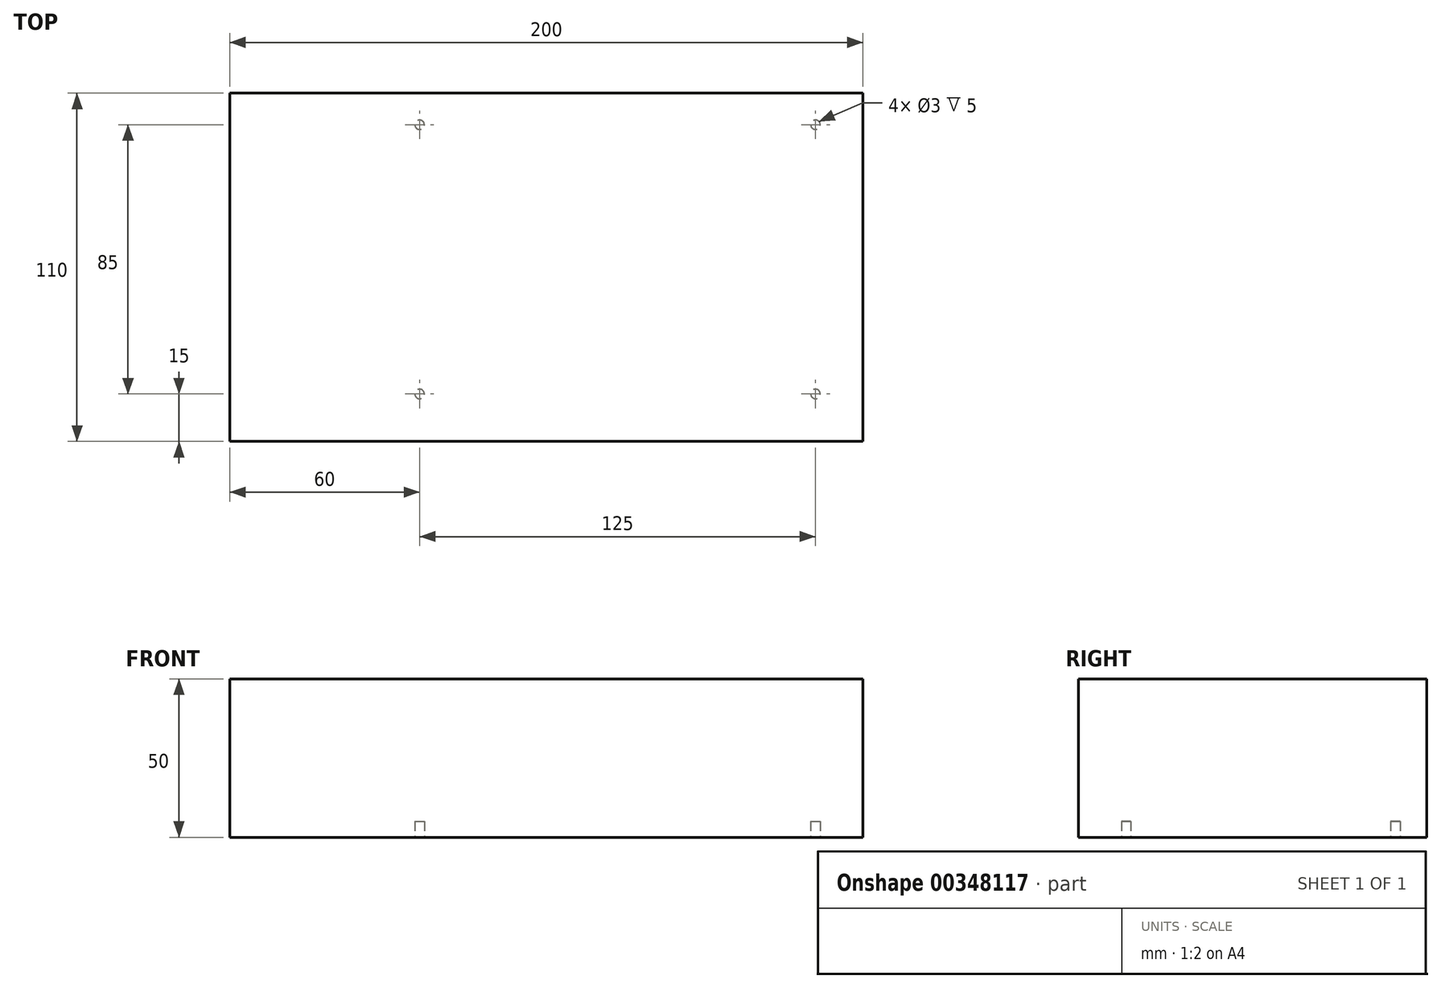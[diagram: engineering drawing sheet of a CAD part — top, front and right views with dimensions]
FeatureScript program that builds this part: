
annotation { "Feature Type Name" : "Feature", "Feature Type Description" : "" }
export const myFeature = defineFeature(function(context is Context, id is Id, definition is map)
    precondition{}
    {
        {
            assignVariable(context, id + "F0", {"name" : "Height", "anyValue" : 50});
        }
        {
            var Q0;
            Q0=qCreatedBy(makeId("Top.planeOp"),FACE);
            var sketch = newSketch(context, id + "F1", { "sketchPlane" : qUnion([Q0])});
            skLineSegment(sketch, "E0.bottom", {"start": v(100, 55) * mm, "end": v(-100, 55) * mm});
            skLineSegment(sketch, "E0.top", {"start": v(100, -55) * mm, "end": v(-100, -55) * mm});
            skLineSegment(sketch, "E0.left", {"start": v(100, 55) * mm, "end": v(100, -55) * mm});
            skLineSegment(sketch, "E0.right", {"start": v(-100, 55) * mm, "end": v(-100, -55) * mm});
            skPoint(sketch, "E0.middle", {"position": v(0, 0) * mm});
            skSolve(sketch);
        }
        {
            var Q0;
            Q0 = qSketchRegion(id + "F1", true);
            extrude(context, id + "F2", {"entities" : qUnion([Q0]), "depth" : (getVariable(context, 'Height')) * mm});
        }
        {
            var Q0;
            Q0=makeQuery(id+"F2.opExtrude","CAP_FACE",FACE,{"disambiguationData":[OSD([sQuery(id+"F1.wireOp",EDGE,"E0.bottom"),sQuery(id+"F1.wireOp",EDGE,"E0.top"),sQuery(id+"F1.wireOp",EDGE,"E0.left"),sQuery(id+"F1.wireOp",EDGE,"E0.right")])],"isStart":true});
            var sketch = newSketch(context, id + "F3", { "sketchPlane" : qUnion([Q0])});
            skPoint(sketch, "E1", {"position": v(-40, -45) * mm});
            skPoint(sketch, "E2.0.1.0", {"position": v(-40, 40) * mm});
            skPoint(sketch, "E2.1.0.0", {"position": v(85, -45) * mm});
            skPoint(sketch, "E2.1.1.0", {"position": v(85, 40) * mm});
            skLineSegment(sketch, "E2.direction1", {"start": v(-40, -45) * mm, "end": v(85, -45) * mm, "construction": true});
            skLineSegment(sketch, "E2.direction2", {"start": v(-40, -45) * mm, "end": v(-40, 40) * mm, "construction": true});
            skCircle(sketch, "E3", {"center": v(-40, 40) * mm, "radius": 1.5 * mm});
            skCircle(sketch, "E4", {"center": v(-40, -45) * mm, "radius": 1.5 * mm});
            skCircle(sketch, "E5", {"center": v(85, -45) * mm, "radius": 1.5 * mm});
            skCircle(sketch, "E6", {"center": v(85, 40) * mm, "radius": 1.5 * mm});
            skSolve(sketch);
        }
        {
            var Q0;
            Q0 = qSketchRegion(id + "F3", true);
            extrude(context, id + "F4", {"entities" : qUnion([Q0]), "operationType" : NewBodyOperationType.REMOVE, "oppositeDirection" : true, "depth" : 5 * mm});
        }
    });
